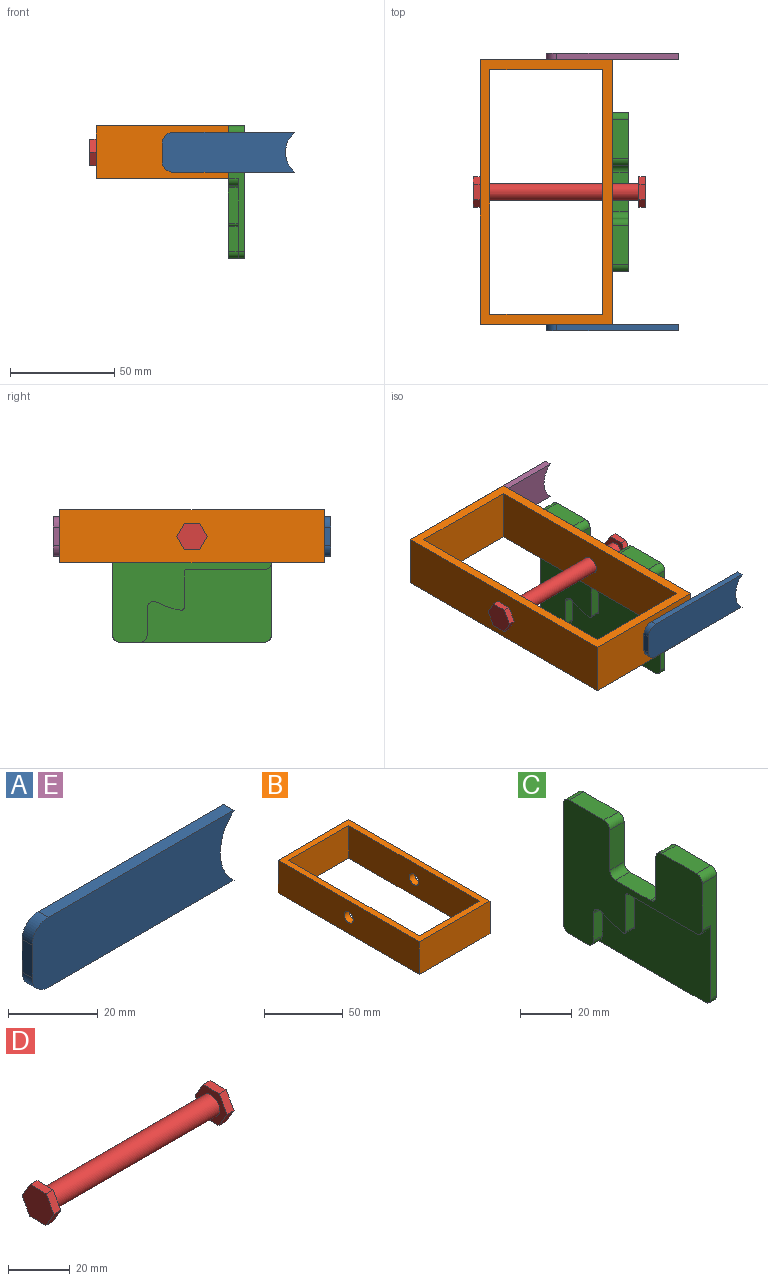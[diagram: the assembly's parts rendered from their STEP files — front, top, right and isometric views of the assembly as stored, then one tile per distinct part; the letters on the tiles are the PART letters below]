
ASSEMBLY  parts=5 mates=4
PART A: 8 faces, bbox 63.5x3.2x19.1 mm
  f0: plane 8.89x3.18mm, normal (-1,0,0), area 28.2mm2, adj f4,f5,f6,f7
  f1: plane 58.42x3.18mm, normal (0,0,-1), area 185.5mm2, adj f2,f4,f5,f6
  f2: cylinder r=12.7mm len=19.05mm, axis (0,1,0), area 68.4mm2, adj f1,f3,f4,f5
  f3: plane 58.42x3.18mm, normal (0,0,1), area 185.5mm2, adj f2,f4,f5,f7
  f4: plane 63.5x19.05mm, normal (0,-1,0), area 1141.8mm2, adj f0,f1,f2,f3,f6,f7
  f5: plane 63.5x19.05mm, normal (0,1,0), area 1141.8mm2, adj f0,f1,f2,f3,f6,f7
  f6: cylinder r=5.08mm len=5.08mm, axis (0,-1,0), area 25.3mm2, adj f0,f1,f4,f5
  f7: cylinder r=5.08mm len=5.08mm, axis (0,1,0), area 25.3mm2, adj f0,f3,f4,f5
PART B: 12 faces, bbox 63.5x127x25.4 mm
  f0: plane 63.5x25.4mm, normal (0,1,0), area 1612.9mm2, adj f1,f7,f8,f9
  f1: plane 127x25.4mm, normal (-1,0,0), area 3171.3mm2, adj f0,f2,f8,f9,f11
  f2: plane 63.5x25.4mm, normal (0,-1,0), area 1612.9mm2, adj f1,f7,f8,f9
  f3: plane 117.6x25.4mm, normal (1,0,0), area 2932.6mm2, adj f4,f6,f8,f9,f11
  f4: plane 54.1x25.4mm, normal (0,-1,0), area 1374.2mm2, adj f3,f5,f8,f9
  f5: plane 117.6x25.4mm, normal (-1,0,0), area 2932.6mm2, adj f4,f6,f8,f9,f10
  f6: plane 54.1x25.4mm, normal (0,1,0), area 1374.2mm2, adj f3,f5,f8,f9
  f7: plane 127x25.4mm, normal (1,0,0), area 3171.3mm2, adj f0,f2,f8,f9,f10
  f8: plane 127x63.5mm, normal (0,0,-1), area 1702mm2, adj f0,f1,f2,f3,f4,f5,f6,f7
  f9: plane 127x63.5mm, normal (0,0,1), area 1702mm2, adj f0,f1,f2,f3,f4,f5,f6,f7
  f10: cylinder r=4.17mm len=8.33mm, axis (1,0,0), area 123mm2, adj f5,f7
  f11: cylinder r=4.17mm len=8.33mm, axis (1,0,0), area 123mm2, adj f1,f3
PART C: 28 faces, bbox 7.9x76.2x63.5 mm
  f0: plane 19.05x7.94mm, normal (0,0,1), area 151.2mm2, adj f7,f12,f15,f27
  f1: plane 62.86x38.1mm, normal (-1,0,0), area 1773.2mm2, adj f4,f5,f6,f18,f19,f20,f21,f22
  f2: plane 57.15x7.94mm, normal (0,1,0), area 453.6mm2, adj f3,f7,f12,f27
  f3: cylinder r=3.17mm len=7.94mm, axis (1,0,0), area 39.6mm2, adj f2,f4,f7,f27
  f4: plane 69.85x7.94mm, normal (0,0,-1), area 270.2mm2, adj f1,f3,f5,f7,f18,f27
  f5: cylinder r=3.17mm len=3.18mm, axis (1,0,0), area 15.8mm2, adj f1,f4,f6,f7
  f6: plane 57.15x7.94mm, normal (0,-1,0), area 287.3mm2, adj f1,f5,f7,f13,f26,f27
  f7: plane 76.2x63.5mm, normal (1,0,0), area 4184.9mm2, adj f0,f2,f3,f4,f5,f6,f8,f9
  f8: plane 19.05x7.94mm, normal (0,0,1), area 151.2mm2, adj f7,f13,f14,f27
  f9: plane 19.05x7.94mm, normal (0,-1,0), area 151.2mm2, adj f7,f15,f17,f27
  f10: plane 19.05x7.94mm, normal (0,1,0), area 151.2mm2, adj f7,f14,f16,f27
  f11: plane 19.05x7.94mm, normal (0,0,1), area 151.2mm2, adj f7,f16,f17,f27
  f12: cylinder r=3.17mm len=7.94mm, axis (-1,0,0), area 39.6mm2, adj f0,f2,f7,f27
  f13: cylinder r=3.17mm len=7.94mm, axis (1,0,0), area 39.6mm2, adj f6,f7,f8,f27
  f14: cylinder r=3.17mm len=7.94mm, axis (-1,0,0), area 39.6mm2, adj f7,f8,f10,f27
  f15: cylinder r=3.17mm len=7.94mm, axis (1,0,0), area 39.6mm2, adj f0,f7,f9,f27
  f16: cylinder r=3.17mm len=7.94mm, axis (1,0,0), area 39.6mm2, adj f7,f10,f11,f27
  f17: cylinder r=3.17mm len=7.94mm, axis (-1,0,0), area 39.6mm2, adj f7,f9,f11,f27
  f18: cylinder r=3.17mm len=4.76mm, axis (1,0,0), area 23.8mm2, adj f1,f4,f19,f27
  f19: plane 13.08x4.76mm, normal (0,-1,0), area 62.3mm2, adj f1,f18,f20,f27
  f20: cylinder r=3.24mm len=4.91mm, axis (1,0,0), area 32.6mm2, adj f1,f19,f21,f27
  f21: cylinder r=35.88mm len=11.51mm, axis (1,0,0), area 57.9mm2, adj f1,f20,f22,f27
  f22: cylinder r=1.19mm len=4.76mm, axis (1,0,0), area 9.7mm2, adj f1,f21,f23,f27
  f23: plane 17.26x4.76mm, normal (0,-1,0), area 82.2mm2, adj f1,f22,f24,f27
  f24: cylinder r=1.19mm len=4.76mm, axis (1,0,0), area 8.9mm2, adj f1,f23,f25,f27
  f25: plane 37.54x4.76mm, normal (0,0,-1), area 178.8mm2, adj f1,f24,f26,f27
  f26: cylinder r=3.17mm len=4.76mm, axis (1,0,0), area 23.8mm2, adj f1,f6,f25,f27
  f27: plane 76.2x63.5mm, normal (-1,0,0), area 2411.7mm2, adj f0,f2,f3,f4,f6,f8,f9,f10
PART D: 17 faces, bbox 82.6x14.7x12.7 mm
  f0: cylinder r=3.97mm len=76.2mm, axis (-1,0,0), area 1900.2mm2, adj f8,f16
  f1: plane 6.33x3.7mm, normal (0,0.86,0.5), area 23.3mm2, adj f2,f6,f7,f8
  f2: plane 7.33x3.18mm, normal (0,-0.01,1), area 23.3mm2, adj f1,f3,f7,f8
  f3: plane 6.37x3.63mm, normal (0,-0.87,0.5), area 23.3mm2, adj f2,f4,f7,f8
  f4: plane 6.33x3.7mm, normal (0,-0.86,-0.5), area 23.3mm2, adj f3,f5,f7,f8
  f5: plane 7.33x3.18mm, normal (0,0.01,-1), area 23.3mm2, adj f4,f6,f7,f8
  f6: plane 6.37x3.63mm, normal (0,0.87,-0.5), area 23.3mm2, adj f1,f5,f7,f8
  f7: plane 14.66x12.74mm, normal (1,0,0), area 139.7mm2, adj f1,f2,f3,f4,f5,f6
  f8: plane 14.66x12.74mm, normal (-1,0,0), area 90.2mm2, adj f0,f1,f2,f3,f4,f5,f6
  f9: plane 6.33x3.7mm, normal (0,0.86,0.5), area 23.3mm2, adj f10,f14,f15,f16
  f10: plane 7.33x3.18mm, normal (0,-0.01,1), area 23.3mm2, adj f9,f11,f15,f16
  f11: plane 6.37x3.63mm, normal (0,-0.87,0.5), area 23.3mm2, adj f10,f12,f15,f16
  f12: plane 6.33x3.7mm, normal (0,-0.86,-0.5), area 23.3mm2, adj f11,f13,f15,f16
  f13: plane 7.33x3.18mm, normal (0,0.01,-1), area 23.3mm2, adj f12,f14,f15,f16
  f14: plane 6.37x3.63mm, normal (0,0.87,-0.5), area 23.3mm2, adj f9,f13,f15,f16
  f15: plane 14.66x12.74mm, normal (-1,0,0), area 139.7mm2, adj f9,f10,f11,f12,f13,f14
  f16: plane 14.66x12.74mm, normal (1,0,0), area 90.2mm2, adj f0,f9,f10,f11,f12,f13,f14
PART E: same geometry as A
PLACE A t=(0,-63.5,-22.23)mm
PLACE B at identity
PLACE C t=(39.69,38.1,-25.4)mm
PLACE D t=(6.35,0,-12.7)mm
PLACE E t=(0,66.68,-22.23)mm
MATE fastened A.f5 <-> B.f2  axis (0,1,0) through (0,-63.5,-12.7)mm
MATE fastened E.f4 <-> B.f0  axis (0,-1,0) through (0,63.5,-12.7)mm
MATE fastened C.f21 <-> B.f10  axis (-1,0,0) through (31.75,0,-12.7)mm
MATE fastened D.f0 <-> B.f10  axis (1,0,0) through (-31.75,0,-12.7)mm
